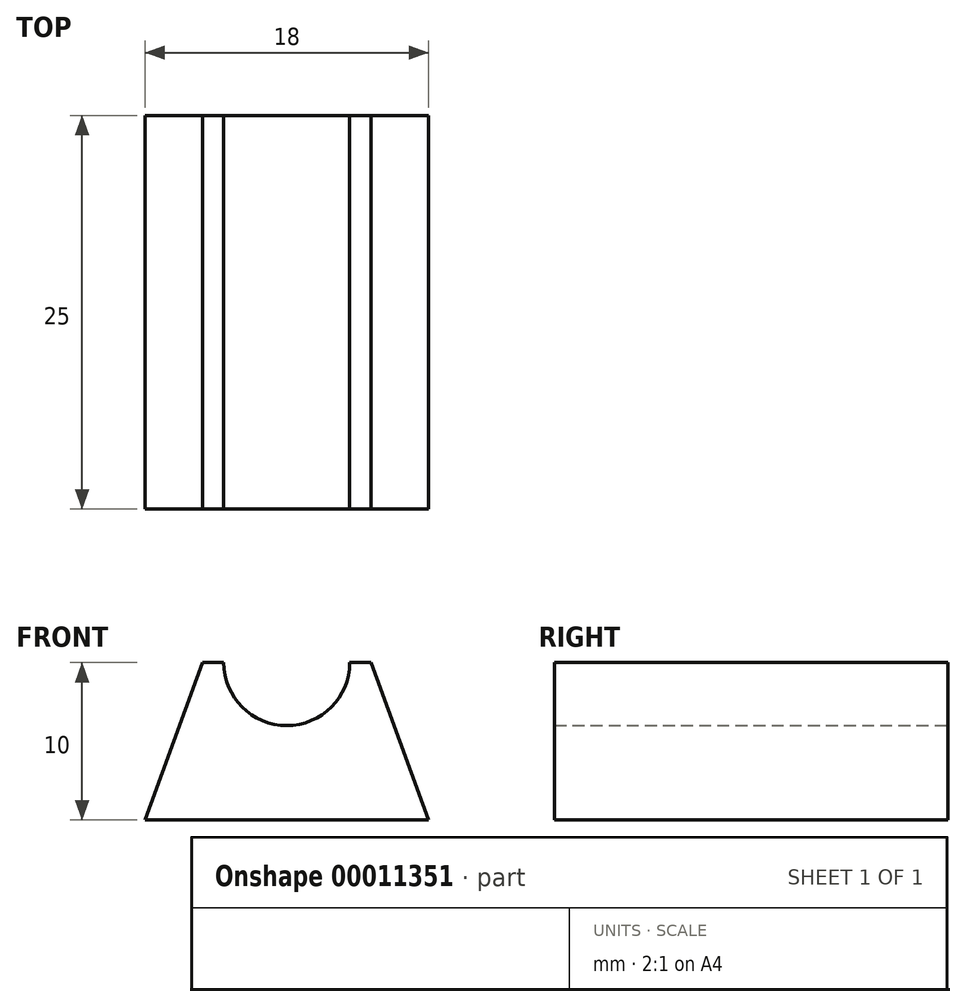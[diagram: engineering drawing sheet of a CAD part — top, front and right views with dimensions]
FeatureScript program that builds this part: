
annotation { "Feature Type Name" : "Feature", "Feature Type Description" : "" }
export const myFeature = defineFeature(function(context is Context, id is Id, definition is map)
    precondition{}
    {
        {
            var Q0;
            Q0=qCreatedBy(makeId("Front.planeOp"),FACE);
            var sketch = newSketch(context, id + "F0", { "sketchPlane" : qUnion([Q0])});
            skArc(sketch, "E0", {"start": v(-4, 0) * mm, "mid": v(0, -4) * mm, "end": v(4, 0) * mm});
            skLineSegment(sketch, "E1", {"start": v(-4, 0) * mm, "end": v(-5.36, 0) * mm});
            skLineSegment(sketch, "E2", {"start": v(-5.36, 0) * mm, "end": v(-9, -10) * mm});
            skLineSegment(sketch, "E3", {"start": v(-9, -10) * mm, "end": v(0, -10) * mm});
            skLineSegment(sketch, "E4.MirrorCS", {"start": v(4, 0) * mm, "end": v(5.36, 0) * mm});
            skLineSegment(sketch, "E5.MirrorCS", {"start": v(9, -10) * mm, "end": v(0, -10) * mm});
            skLineSegment(sketch, "E6.MirrorCS", {"start": v(5.36, 0) * mm, "end": v(9, -10) * mm});
            skSolve(sketch);
        }
        {
            var Q0;
            Q0=makeQuery(id+"F0.imprint","IMPRINT",FACE,{"disambiguationData":[TD([[makeQuery(id+"F0.imprint","IMPRINT",EDGE,{"derivedFrom":sQuery(id+"F0.wireOp",EDGE,"E0")}),-1.0]])]});
            extrude(context, id + "F1", {"entities" : qUnion([Q0]), "depth" : 25 * mm, "symmetric" : true});
        }
    });
